# Revit family: Electrical-Teknion-MXPBP_Below_Power_Module-R2023
name_source: partatom
category: Furniture
units: mm (PartAtom-declared; Revit-internal decimal feet)

## family parameters
Always vertical = Yes
Cut with Voids When Loaded = No
Enable Cutting in Views = No
OmniClass Number = 23.40.20.00
OmniClass Title = General Furniture and Specialties
Render Appearance Source = Family Geometry
Room Calculation Point = No
Shared = Yes
Work Plane-Based = No

## types (4) — shared parameters
Assembly Code = E2020200
Manufacturer = Teknion
Manufacturer Fax = 416.661.4586
Part Number = MXPBP
Product Documentation Link = http://www.teknion.com
Product Line = Electrical/Accesories
Product Page URL = http://www.teknion.com
Series = Expansion Meeting
Sustainability Data = https://www.teknion.com
URL = www.teknion.com
Unit Weight URL = http://www.teknion.com
Warranty = http://www.teknion.com
zero-valued in all types: Default Elevation

## per-type parameters (varying)
| type | Description | Front - HDMI | Front - Power 1 | Front - Power 2 | Front - USB (18W) | Front - USB (65W) | Model | RA - 1 Power/ 1 USB - A+C (65W)/ 1 Power (Rear) | RB - 1 Power/ 1 USB - A+C (18W)/ 1 Power (Rear) | RC - 2 Power/ 1 Power (Rear) | RD - 1 Power/ 1 HDMI/ 1 HDMI (Rear) | Rear - HDMI | Rear - Power |
| 1 Power/ 1 USB - A+C (65W)/ 1 Power (Rear) | Below Power Module, Standard Plug-In, Standard Undermount, 1 Power/ 1 USB - A+C (65W)/ 1 Power (Rear) Configuration | No | No | Yes | No | Yes | MXPBP_URA_ | Yes | No | No | No | No | Yes |
| 1 Power/ 1 USB - A+C (18W)/ 1 Power (Rear) | Below Power Module, Standard Plug-In, Standard Undermount, 1 Power/ 1 USB - A+C (18W)/ 1 Power (Rear) Configuration | No | No | Yes | Yes | No | MXPBP_URB_ | No | Yes | No | No | No | Yes |
| 2 Power/ 1 Power (Rear) | Below Power Module, Standard Plug-In, Standard Undermount, 2 Power/ 1 Power (Rear) Configuration | No | Yes | Yes | No | No | MXPBP_URC_ | No | No | Yes | No | No | Yes |
| 1 Power/ 1 HDMI/ 1 HDMI (Rear) | Below Power Module, Standard Plug-In, Standard Undermount, 1 Power/ 1 HDMI/ 1 HDMI (Rear) Configuration | Yes | Yes | No | No | No | MXPBP_URD_ | No | No | No | Yes | Yes | No |

## geometry (parser evidence)
native form markers: Sweep x9
no freeform markers — native parametric forms only
